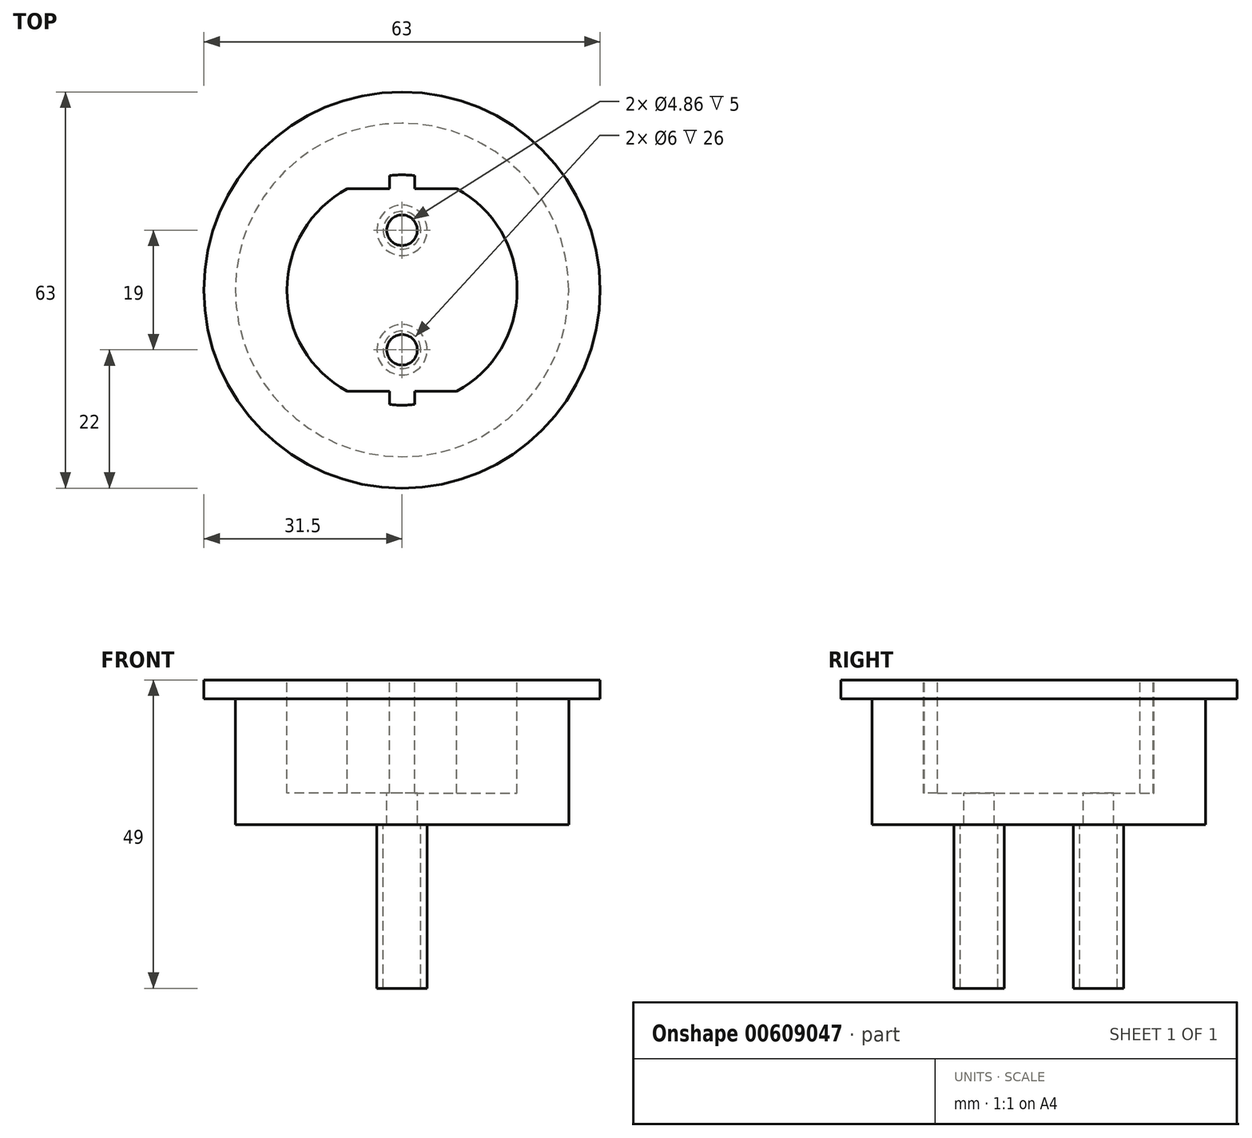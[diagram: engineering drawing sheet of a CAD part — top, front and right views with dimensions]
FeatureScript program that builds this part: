
annotation { "Feature Type Name" : "Feature", "Feature Type Description" : "" }
export const myFeature = defineFeature(function(context is Context, id is Id, definition is map)
    precondition{}
    {
        {
            var Q0;
            Q0=qCreatedBy(makeId("Front.planeOp"),FACE);
            var sketch = newSketch(context, id + "F0", { "sketchPlane" : qUnion([Q0])});
            skLineSegment(sketch, "E0", {"start": v(0, 0) * mm, "end": v(0, 29) * mm});
            skLineSegment(sketch, "E1", {"start": v(0, 29) * mm, "end": v(31.5, 29) * mm});
            skLineSegment(sketch, "E2", {"start": v(31.5, 29) * mm, "end": v(31.5, 26) * mm});
            skLineSegment(sketch, "E3", {"start": v(31.5, 26) * mm, "end": v(26.5, 26) * mm});
            skLineSegment(sketch, "E4", {"start": v(0, 29) * mm, "end": v(0, 6) * mm});
            skLineSegment(sketch, "E5", {"start": v(0, 6) * mm, "end": v(26.5, 6) * mm});
            skPoint(sketch, "E5.endSnap0", {"position": v(26.5, 13) * mm});
            skLineSegment(sketch, "E6", {"start": v(26.5, 26) * mm, "end": v(26.5, 6) * mm});
            skSolve(sketch);
        }
        {
            var Q0;
            Q0=makeQuery(id+"F0.imprint","IMPRINT",FACE,{"disambiguationData":[TD([[makeQuery(id+"F0.imprint","IMPRINT",EDGE,{"derivedFrom":sQuery(id+"F0.wireOp",EDGE,"E1")}),-1.0]])]});
            var Q1;
            Q1=sQuery(id+"F0.wireOp",EDGE,"E0");
            revolve(context, id + "F1", {"entities" : qUnion([Q0]), "axis" : qUnion([Q1]), "revolveType" : RevolveType.FULL});
        }
        {
            var Q0;
            Q0=makeQuery(id+"F1.opRevolve","SWEPT_FACE",FACE,{"disambiguationData":[OSD([sQuery(id+"F0.wireOp",EDGE,"E1")])]});
            var sketch = newSketch(context, id + "F2", { "sketchPlane" : qUnion([Q0])});
            skLineSegment(sketch, "E7", {"start": v(0, 0) * mm, "end": v(18.3, 0) * mm});
            skLineSegment(sketch, "E8", {"start": v(0, 0) * mm, "end": v(0, 16.1) * mm});
            skCircle(sketch, "E9", {"center": v(0, 0) * mm, "radius": 18.3 * mm});
            skLineSegment(sketch, "E10", {"start": v(0, 0) * mm, "end": v(0, -16.1) * mm});
            skLineSegment(sketch, "E11", {"start": v(8.7, 16.1) * mm, "end": v(-8.7, 16.1) * mm});
            skLineSegment(sketch, "E12", {"start": v(0, -16.1) * mm, "end": v(8.7, -16.1) * mm});
            skLineSegment(sketch, "E13", {"start": v(8.7, -16.1) * mm, "end": v(0, -16.1) * mm});
            skLineSegment(sketch, "E14", {"start": v(-8.7, -16.1) * mm, "end": v(0, -16.1) * mm});
            skLineSegment(sketch, "E15", {"start": v(0, 0) * mm, "end": v(0, 9.5) * mm});
            skLineSegment(sketch, "E16", {"start": v(0, 0) * mm, "end": v(0, -9.5) * mm});
            skLineSegment(sketch, "E17", {"start": v(-2, 16.1) * mm, "end": v(2, 16.1) * mm});
            skLineSegment(sketch, "E18", {"start": v(-2, -16.1) * mm, "end": v(2, -16.1) * mm});
            skLineSegment(sketch, "E19", {"start": v(-2, 16.1) * mm, "end": v(-2, 18.2) * mm});
            skLineSegment(sketch, "E20", {"start": v(2, 16.1) * mm, "end": v(2, 18.2) * mm});
            skLineSegment(sketch, "E21", {"start": v(-2, -16.1) * mm, "end": v(-2, -18.2) * mm});
            skLineSegment(sketch, "E22", {"start": v(2, -16.1) * mm, "end": v(2, -18.2) * mm});
            skLineSegment(sketch, "E23", {"start": v(0, 0) * mm, "end": v(10, 0) * mm});
            skSolve(sketch);
        }
        {
            var Q0;
            {var subQ0=sQuery(id+"F2.wireOp",EDGE,"E21");Q0=makeQuery(id+"F2.imprint","IMPRINT",FACE,{"disambiguationData":[TD([[makeQuery(id+"F2.imprint","IMPRINT",EDGE,{"derivedFrom":subQ0}),1.0]])]});}
            var Q1;
            {var subQ7=sQuery(id+"F2.wireOp",EDGE,"E8");Q1=makeQuery(id+"F2.imprint","IMPRINT",FACE,{"disambiguationData":[TD([[makeQuery(id+"F2.imprint","IMPRINT",EDGE,{"derivedFrom":subQ7}),1.0]])]});}
            var Q2;
            {var subQ0=sQuery(id+"F2.wireOp",EDGE,"E19");Q2=makeQuery(id+"F2.imprint","IMPRINT",FACE,{"disambiguationData":[TD([[makeQuery(id+"F2.imprint","IMPRINT",EDGE,{"derivedFrom":subQ0}),-1.0]])]});}
            var Q3;
            {var subQ6=sQuery(id+"F2.wireOp",EDGE,"E7");Q3=makeQuery(id+"F2.imprint","IMPRINT",FACE,{"disambiguationData":[TD([[makeQuery(id+"F2.imprint","IMPRINT",EDGE,{"derivedFrom":subQ6}),1.0]])]});}
            var Q4;
            {var subQ2=sQuery(id+"F2.wireOp",EDGE,"E7");Q4=makeQuery(id+"F2.imprint","IMPRINT",FACE,{"disambiguationData":[TD([[makeQuery(id+"F2.imprint","IMPRINT",EDGE,{"derivedFrom":subQ2}),-1.0]])]});}
            extrude(context, id + "F3", {"entities" : qUnion([Q0, Q1, Q2, Q3, Q4]), "operationType" : NewBodyOperationType.REMOVE, "oppositeDirection" : true, "depth" : 18 * mm, "offsetDistance" : 25 * mm});
        }
        {
            var Q0;
            Q0=sQuery(id+"F2.wireOp",VERTEX,"E15.end");
            var Q1;
            Q1=sQuery(id+"F2.wireOp",VERTEX,"E16.end");
            var Q2;
            Q2=makeQuery(id+"F1.opRevolve","SWEPT_BODY",BODY,{"disambiguationData":[OSD([sQuery(id+"F0.wireOp",EDGE,"E0"),sQuery(id+"F0.wireOp",EDGE,"E1"),sQuery(id+"F0.wireOp",EDGE,"E2"),sQuery(id+"F0.wireOp",EDGE,"E3"),sQuery(id+"F0.wireOp",EDGE,"YAWO67Hd-5U8C-U3rc-iRtI-eKS0pJLDJjBz"),sQuery(id+"F0.wireOp",EDGE,"WrtkL62Z-Nl6X-ohxe-ayLN-IRGdZlgAnF6L")])]});
            hole(context, id + "F4", {"style" : HoleStyle.SIMPLE, "endStyle" : HoleEndStyle.THROUGH, "holeDiameter" : 4.86 * mm, "majorDiameter" : 5 * mm, "isTappedThrough" : true, "tappedDepth" : 12 * mm, "tapClearance" : 3, "locations" : qUnion([Q0, Q1]), "scope" : qUnion([Q2])});
        }
        {
            var Q0;
            Q0=makeQuery(id+"F1.opRevolve","SWEPT_FACE",FACE,{"disambiguationData":[OSD([sQuery(id+"F0.wireOp",EDGE,"E5")])]});
            var sketch = newSketch(context, id + "F5", { "sketchPlane" : qUnion([Q0])});
            skLineSegment(sketch, "E24", {"start": v(0, 9.5) * mm, "end": v(-3, 9.5) * mm});
            skLineSegment(sketch, "E25", {"start": v(-3, 9.5) * mm, "end": v(-4, 9.5) * mm});
            skCircle(sketch, "E26", {"center": v(0, 9.5) * mm, "radius": 3 * mm});
            skCircle(sketch, "E27", {"center": v(0, 9.5) * mm, "radius": 4 * mm});
            skLineSegment(sketch, "E28", {"start": v(0, -9.5) * mm, "end": v(-3, -9.5) * mm});
            skLineSegment(sketch, "E29", {"start": v(-3, -9.5) * mm, "end": v(-4, -9.5) * mm});
            skCircle(sketch, "E30", {"center": v(0, -9.5) * mm, "radius": 3 * mm});
            skCircle(sketch, "E31", {"center": v(0, -9.5) * mm, "radius": 4 * mm});
            skSolve(sketch);
        }
        {
            var Q0;
            Q0=qSketchRegion(id+"F5",true);
            extrude(context, id + "F6", {"entities" : qUnion([Q0]), "operationType" : NewBodyOperationType.ADD, "depth" : 26 * mm, "offsetDistance" : 25 * mm});
        }
    });
